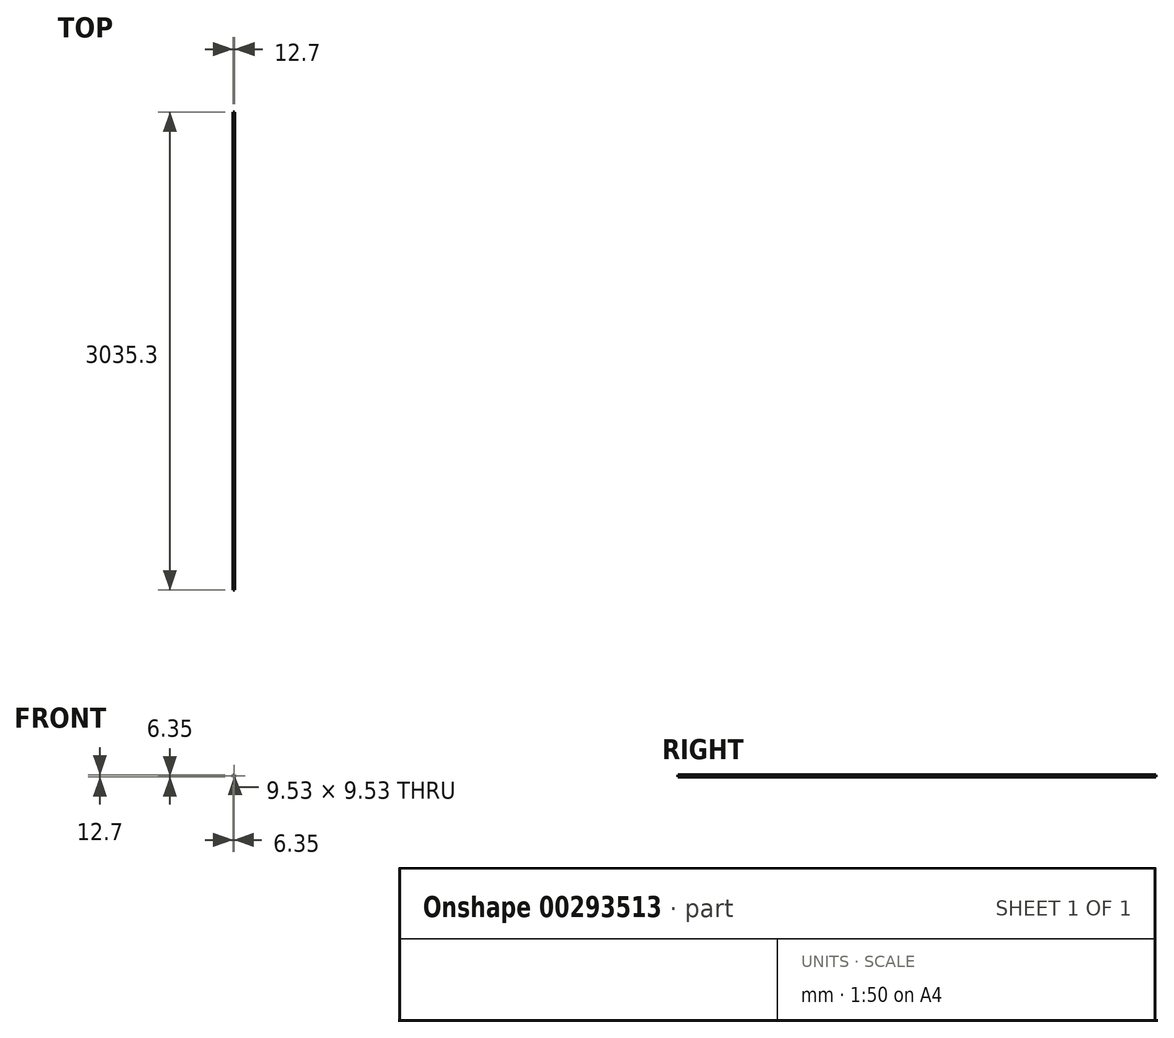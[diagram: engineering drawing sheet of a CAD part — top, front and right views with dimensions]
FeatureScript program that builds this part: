
annotation { "Feature Type Name" : "Feature", "Feature Type Description" : "" }
export const myFeature = defineFeature(function(context is Context, id is Id, definition is map)
    precondition{}
    {
        {
            var Q0;
            Q0=qCreatedBy(makeId("Front.planeOp"),FACE);
            var sketch = newSketch(context, id + "F0", { "sketchPlane" : qUnion([Q0])});
            skLineSegment(sketch, "E0.bottom", {"start": v(6.35, 6.35) * mm, "end": v(-6.35, 6.35) * mm});
            skLineSegment(sketch, "E0.top", {"start": v(6.35, -6.35) * mm, "end": v(-6.35, -6.35) * mm});
            skLineSegment(sketch, "E0.left", {"start": v(6.35, 6.35) * mm, "end": v(6.35, -6.35) * mm});
            skLineSegment(sketch, "E0.right", {"start": v(-6.35, 6.35) * mm, "end": v(-6.35, -6.35) * mm});
            skPoint(sketch, "E0.middle", {"position": v(0, 0) * mm});
            skLineSegment(sketch, "E1.bottom", {"start": v(4.76, 4.76) * mm, "end": v(-4.76, 4.76) * mm});
            skLineSegment(sketch, "E1.top", {"start": v(4.76, -4.76) * mm, "end": v(-4.76, -4.76) * mm});
            skLineSegment(sketch, "E1.left", {"start": v(4.76, 4.76) * mm, "end": v(4.76, -4.76) * mm});
            skLineSegment(sketch, "E1.right", {"start": v(-4.76, 4.76) * mm, "end": v(-4.76, -4.76) * mm});
            skSolve(sketch);
        }
        {
            var Q0;
            Q0 = qSketchRegion(id + "F0", true);
            extrude(context, id + "F1", {"entities" : qUnion([Q0]), "endBound" : BoundingType.SYMMETRIC, "depth" : 3035.3 * mm});
        }
    });
